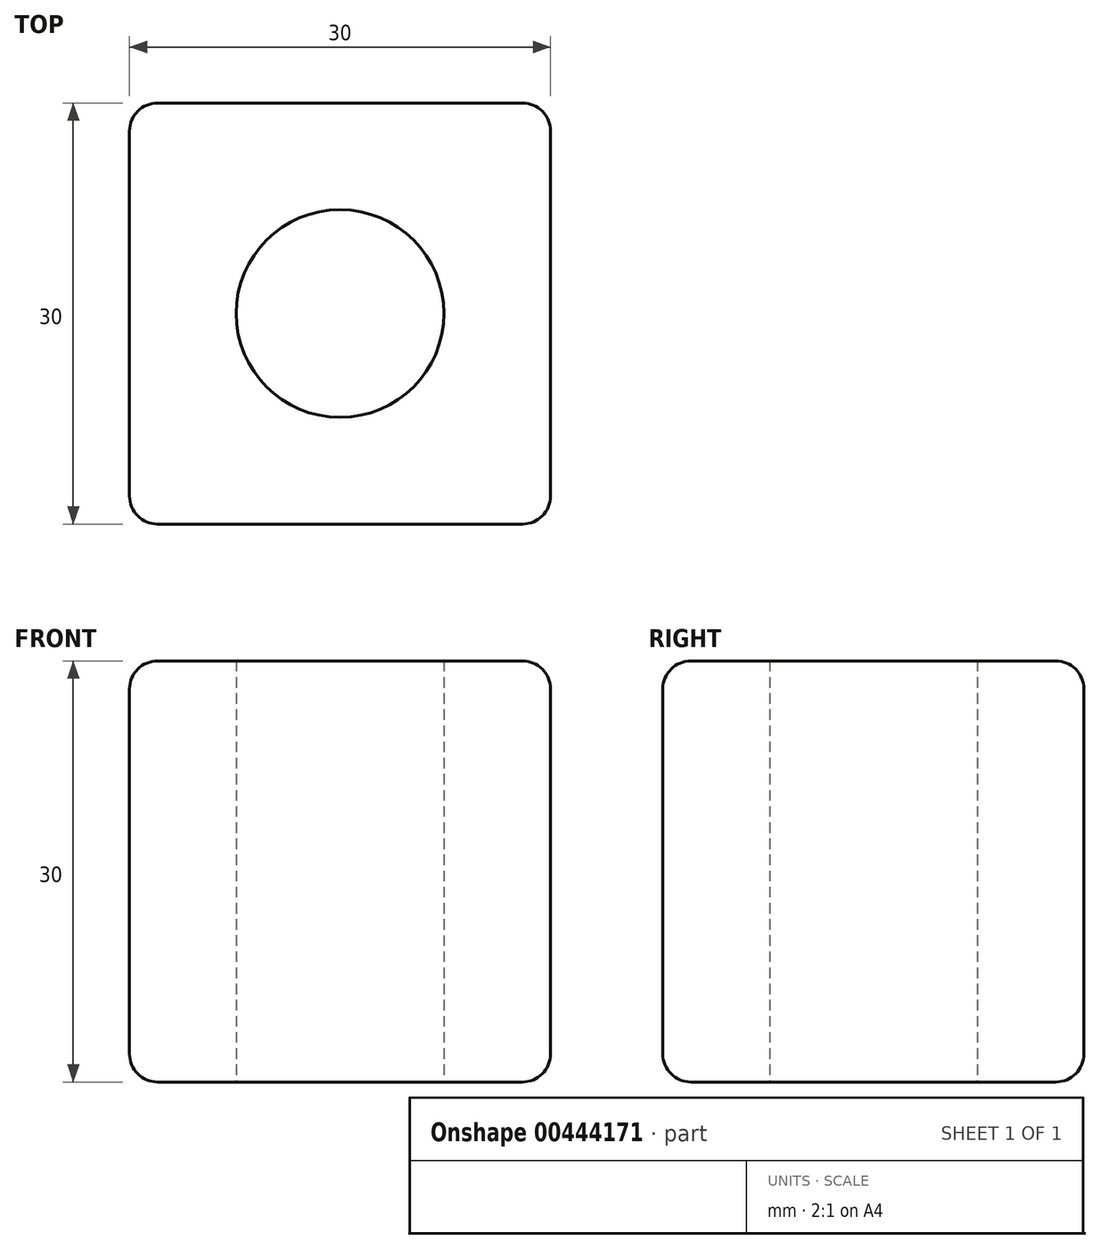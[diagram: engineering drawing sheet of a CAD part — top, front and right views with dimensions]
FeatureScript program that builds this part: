
annotation { "Feature Type Name" : "Feature", "Feature Type Description" : "" }
export const myFeature = defineFeature(function(context is Context, id is Id, definition is map)
    precondition{}
    {
        {
            var Q0;
            Q0=qCreatedBy(makeId("Top.planeOp"),FACE);
            var sketch = newSketch(context, id + "F0", { "sketchPlane" : qUnion([Q0])});
            skLineSegment(sketch, "E0.bottom", {"start": v(-13.03, -4.99) * mm, "end": v(16.97, -4.99) * mm});
            skLineSegment(sketch, "E0.top", {"start": v(-13.03, -34.99) * mm, "end": v(16.97, -34.99) * mm});
            skLineSegment(sketch, "E0.left", {"start": v(-13.03, -4.99) * mm, "end": v(-13.03, -34.99) * mm});
            skLineSegment(sketch, "E0.right", {"start": v(16.97, -4.99) * mm, "end": v(16.97, -34.99) * mm});
            skCircle(sketch, "E1", {"center": v(1.97, -19.99) * mm, "radius": 7.4 * mm});
            skSolve(sketch);
        }
        {
            var Q0;
            Q0=makeQuery(id+"F0.imprint","IMPRINT",FACE,{"disambiguationData":[TD([[makeQuery(id+"F0.imprint","IMPRINT",EDGE,{"derivedFrom":sQuery(id+"F0.wireOp",EDGE,"E0.bottom")}),-1.0]])]});
            extrude(context, id + "F1", {"entities" : qUnion([Q0]), "depth" : 30 * mm});
        }
        {
            var Q0;
            Q0=makeQuery(id+"F1.opExtrude","CAP_EDGE",EDGE,{"disambiguationData":[OSD([sQuery(id+"F0.wireOp",EDGE,"E0.top")])],"isStart":false});
            var Q1;
            Q1=makeQuery(id+"F1.opExtrude","CAP_EDGE",EDGE,{"disambiguationData":[OSD([sQuery(id+"F0.wireOp",EDGE,"E0.right")])],"isStart":false});
            var Q2;
            Q2=makeQuery(id+"F1.opExtrude","CAP_EDGE",EDGE,{"disambiguationData":[OSD([sQuery(id+"F0.wireOp",EDGE,"E0.bottom")])],"isStart":false});
            var Q3;
            Q3=makeQuery(id+"F1.opExtrude","CAP_EDGE",EDGE,{"disambiguationData":[OSD([sQuery(id+"F0.wireOp",EDGE,"E0.left")])],"isStart":false});
            var Q4;
            Q4=makeQuery(id+"F1.opExtrude","CAP_EDGE",EDGE,{"disambiguationData":[OSD([sQuery(id+"F0.wireOp",EDGE,"E0.top")])],"isStart":true});
            var Q5;
            Q5=makeQuery(id+"F1.opExtrude","CAP_EDGE",EDGE,{"disambiguationData":[OSD([sQuery(id+"F0.wireOp",EDGE,"E0.left")])],"isStart":true});
            var Q6;
            Q6=makeQuery(id+"F1.opExtrude","CAP_EDGE",EDGE,{"disambiguationData":[OSD([sQuery(id+"F0.wireOp",EDGE,"E0.bottom")])],"isStart":true});
            var Q7;
            Q7=makeQuery(id+"F1.opExtrude","CAP_EDGE",EDGE,{"disambiguationData":[OSD([sQuery(id+"F0.wireOp",EDGE,"E0.right")])],"isStart":true});
            var Q8;
            Q8=makeQuery(id+"F1.opExtrude","SWEPT_EDGE",EDGE,{"disambiguationData":[OSD([sQuery(id+"F0.wireOp",EDGE,"E0.bottom"),sQuery(id+"F0.wireOp",EDGE,"E0.left")])]});
            var Q9;
            Q9=makeQuery(id+"F1.opExtrude","SWEPT_EDGE",EDGE,{"disambiguationData":[OSD([sQuery(id+"F0.wireOp",EDGE,"E0.bottom"),sQuery(id+"F0.wireOp",EDGE,"E0.right")])]});
            var Q10;
            Q10=makeQuery(id+"F1.opExtrude","SWEPT_EDGE",EDGE,{"disambiguationData":[OSD([sQuery(id+"F0.wireOp",EDGE,"E0.top"),sQuery(id+"F0.wireOp",EDGE,"E0.right")])]});
            var Q11;
            Q11=makeQuery(id+"F1.opExtrude","SWEPT_EDGE",EDGE,{"disambiguationData":[OSD([sQuery(id+"F0.wireOp",EDGE,"E0.top"),sQuery(id+"F0.wireOp",EDGE,"E0.left")])]});
            fillet(context, id + "F2", {"entities" : qUnion([Q0, Q1, Q2, Q3, Q4, Q5, Q6, Q7, Q8, Q9, Q10, Q11]), "radius" : 2 * mm, "tangentPropagation" : true, "allowEdgeOverflow" : false});
        }
    });
